# Revit family: 208_91d717cef4b44c1d942cbf9baed58d
name_source: partatom
category: Air Terminals
units: mm (PartAtom-declared; Revit-internal decimal feet)

## family parameters
Always vertical = Yes
Cut with Voids When Loaded = No
Part Type = Normal
Room Calculation Point = Yes
Round Connector Dimension = Use Diameter
Shared = No
Work Plane-Based = No

## types (1)
- 100-400083
    CLBTZ = 0 mm  [stored 0 ft]
    CL_Location_5000 = 5000 mm  [stored 16.4042 ft]
    D = 100 mm
    DT2 = 50 mm  [stored 0.164042 ft]
    Description = Gravity grille MW white
    H1 = 15 mm  [stored 0.0492126 ft]
    H2 = 30 mm  [stored 0.0984252 ft]
    HT2 = 76 mm
    H_ARR = 0 mm  [stored 0 ft]
    L1 = 34 mm  [stored 0.111549 ft]
    L3 = 8 mm  [stored 0.0262467 ft]
    L3__ve = -8 mm
    L4 = 10 mm  [stored 0.0328084 ft]
    L_ARR = 400 mm  [stored 1.31234 ft]
    MC Product Code = 100-400083
    Manufacturer = Flexit
    QmdConnectorList = 201;D
    W1 = 140 mm  [stored 0.459318 ft]
    WT2 = 78 mm  [stored 0.255906 ft]
    W_ARR = 400 mm  [stored 1.31234 ft]
    magiPartTypeId = 208
    magiProductFamilyId = 91d717cef4b44c1d942cbf9baed58d
    magiProductId = 368705dd0e3d475fb6272fc383b9cc

note: [stored X ft] marks values corroborated as IEEE doubles in the binary element streams (Revit-internal decimal feet)

## geometry (parser evidence)
native form markers: Sweep x2
no freeform markers — native parametric forms only
